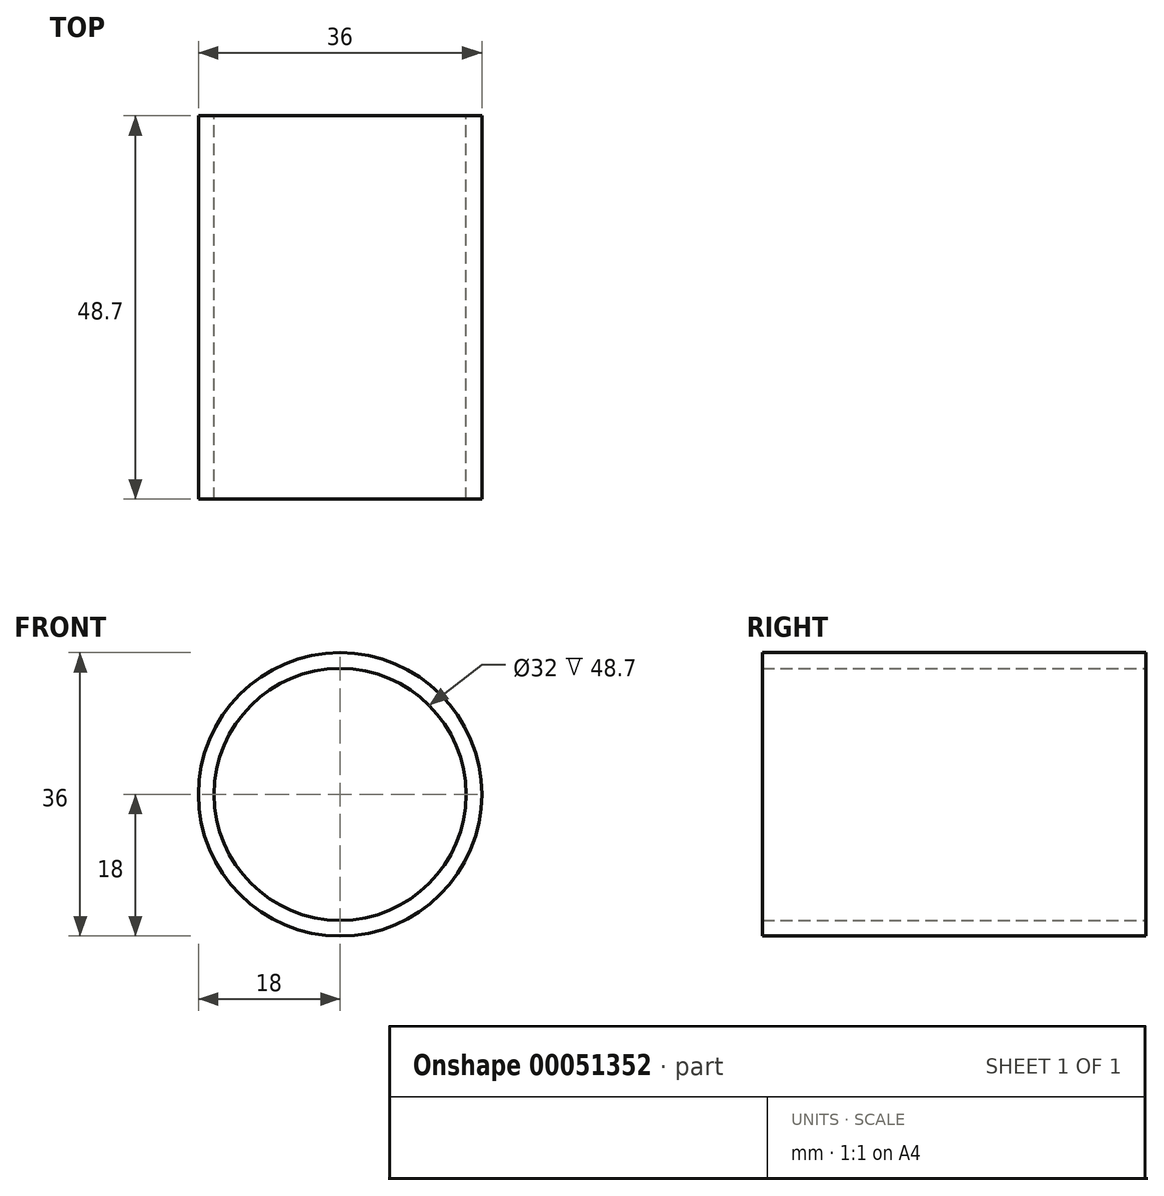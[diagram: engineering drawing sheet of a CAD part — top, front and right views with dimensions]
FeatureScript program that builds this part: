
annotation { "Feature Type Name" : "Feature", "Feature Type Description" : "" }
export const myFeature = defineFeature(function(context is Context, id is Id, definition is map)
    precondition{}
    {
        {
            var Q0;
            Q0=qCreatedBy(makeId("Front.planeOp"),FACE);
            var sketch = newSketch(context, id + "F0", { "sketchPlane" : qUnion([Q0])});
            skCircle(sketch, "E0", {"center": v(0, 0) * mm, "radius": 16 * mm});
            skCircle(sketch, "E1", {"center": v(0, 0) * mm, "radius": 18 * mm});
            skSolve(sketch);
        }
        {
            var Q0;
            Q0 = qSketchRegion(id + "F0", true);
            extrude(context, id + "F1", {"entities" : qUnion([Q0]), "depth" : (59.2 - 6 - 4.5) * mm, "symmetric" : true});
        }
    });
